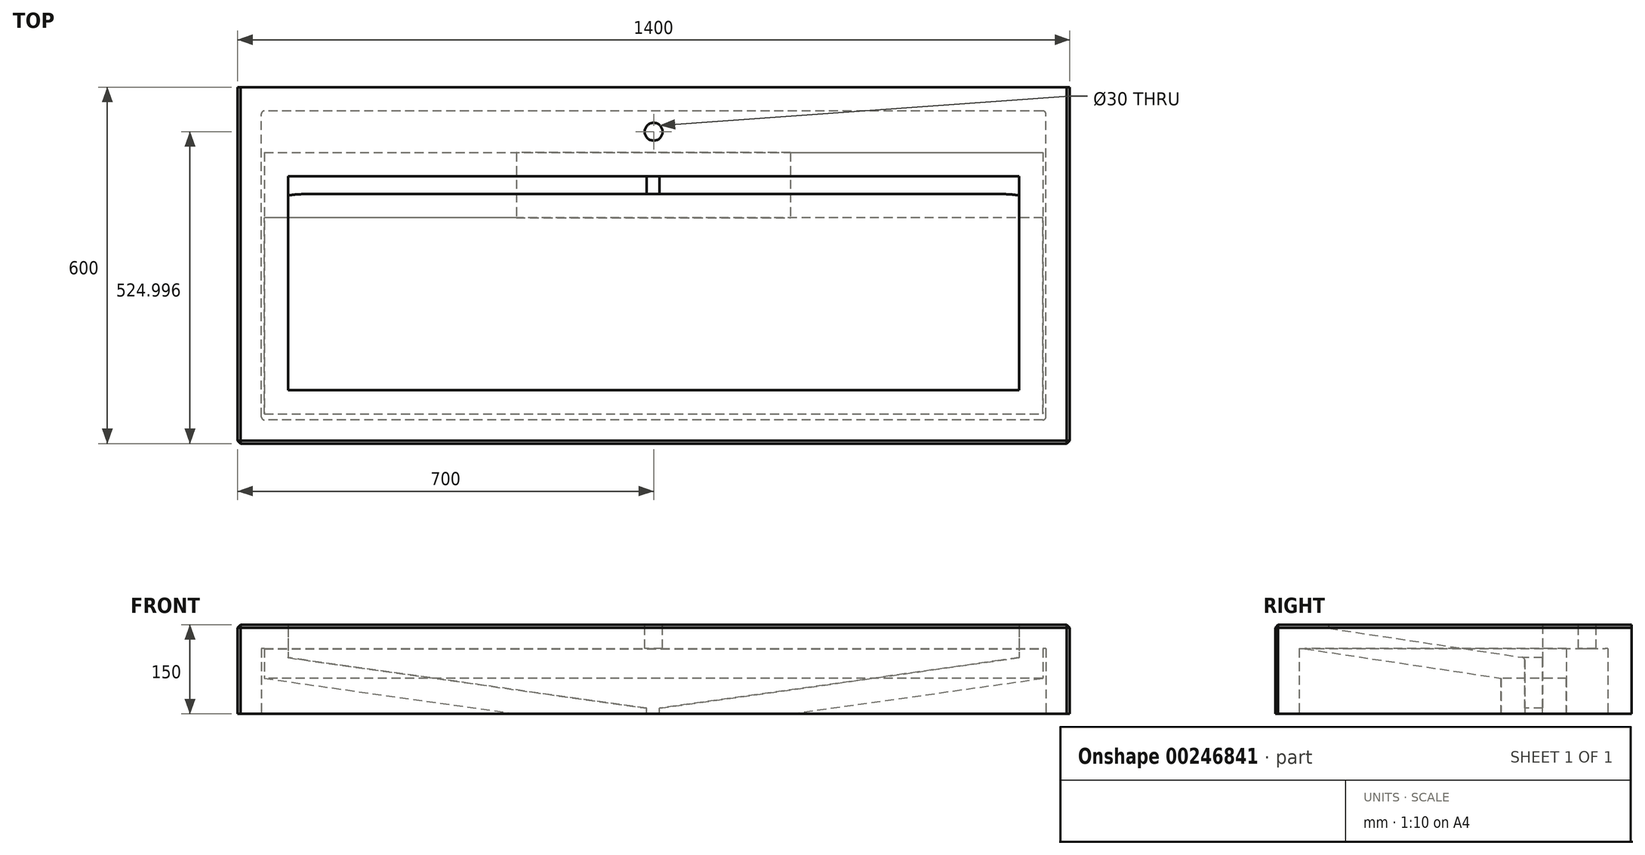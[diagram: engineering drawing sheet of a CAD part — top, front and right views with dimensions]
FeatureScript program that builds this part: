
annotation { "Feature Type Name" : "Feature", "Feature Type Description" : "" }
export const myFeature = defineFeature(function(context is Context, id is Id, definition is map)
    precondition{}
    {
        {
            var Q0;
            Q0=qCreatedBy(makeId("Top.planeOp"),FACE);
            var sketch = newSketch(context, id + "F0", { "sketchPlane" : qUnion([Q0])});
            skLineSegment(sketch, "E0.bottom", {"start": v(700, -284.74) * mm, "end": v(-700, -284.74) * mm});
            skLineSegment(sketch, "E0.top", {"start": v(700, 315.26) * mm, "end": v(-700, 315.26) * mm});
            skLineSegment(sketch, "E0.left", {"start": v(700, -284.74) * mm, "end": v(700, 315.26) * mm});
            skLineSegment(sketch, "E0.right", {"start": v(-700, -284.74) * mm, "end": v(-700, 315.26) * mm});
            skPoint(sketch, "E0.middle", {"position": v(0, 15.26) * mm});
            skSolve(sketch);
        }
        {
            var Q0;
            Q0 = qSketchRegion(id + "F0", true);
            extrude(context, id + "F1", {"entities" : qUnion([Q0]), "depth" : 150 * mm});
        }
        {
            var Q0;
            Q0=makeQuery(id+"F1.opExtrude","CAP_FACE",FACE,{"disambiguationData":[OSD([sQuery(id+"F0.wireOp",EDGE,"E0.bottom"),sQuery(id+"F0.wireOp",EDGE,"E0.top"),sQuery(id+"F0.wireOp",EDGE,"E0.left"),sQuery(id+"F0.wireOp",EDGE,"E0.right")])],"isStart":false});
            var sketch = newSketch(context, id + "F2", { "sketchPlane" : qUnion([Q0])});
            skLineSegment(sketch, "E1.bottom", {"start": v(615, 165.26) * mm, "end": v(-615, 165.26) * mm});
            skLineSegment(sketch, "E1.top", {"start": v(615, -194.74) * mm, "end": v(-615, -194.74) * mm});
            skLineSegment(sketch, "E1.left", {"start": v(615, 165.26) * mm, "end": v(615, -194.74) * mm});
            skLineSegment(sketch, "E1.right", {"start": v(-615, 165.26) * mm, "end": v(-615, -194.74) * mm});
            skLineSegment(sketch, "E2.0", {"start": v(700, 315.26) * mm, "end": v(-700, 315.26) * mm});
            skSolve(sketch);
        }
        {
            var Q0;
            Q0=qCreatedBy(makeId("Right.planeOp"),FACE);
            var Q1;
            Q1=sQuery(id+"F2.wireOp",VERTEX,"E1.bottom.start");
            cPlane(context, id + "F3", {"entities" : qUnion([Q0, Q1]), "cplaneType" : CPlaneType.PLANE_POINT, "offset" : 25 * mm, "width" : 150 * mm, "height" : 150 * mm});
        }
        {
            var Q0;
            Q0=qCreatedBy(id+"F3.planeOp",FACE);
            var sketch = newSketch(context, id + "F4", { "sketchPlane" : qUnion([Q0])});
            skLineSegment(sketch, "E3.0", {"start": v(165.26, 150) * mm, "end": v(-194.74, 150) * mm});
            skLineSegment(sketch, "E4", {"start": v(-194.74, 150) * mm, "end": v(-194.74, 144) * mm});
            skLineSegment(sketch, "E5", {"start": v(165.26, 150) * mm, "end": v(165.26, 90) * mm});
            skLineSegment(sketch, "E6", {"start": v(-194.74, 144) * mm, "end": v(165.26, 90) * mm});
            skSolve(sketch);
        }
        {
            var Q0;
            Q0 = qSketchRegion(id + "F4", true);
            extrude(context, id + "F5", {"entities" : qUnion([Q0]), "operationType" : NewBodyOperationType.REMOVE, "oppositeDirection" : true, "depth" : 1230 * mm});
        }
        {
            var Q0;
            Q0=makeQuery(id+"F2.imprint","IMPRINT",FACE,{"disambiguationData":[TD([[makeQuery(id+"F2.imprint","IMPRINT",EDGE,{"derivedFrom":sQuery(id+"F2.wireOp",EDGE,"E1.bottom")}),1.0]])]});
            var sketch = newSketch(context, id + "F6", { "sketchPlane" : qUnion([Q0])});
            skLineSegment(sketch, "E7.bottom", {"start": v(-615, 165.26) * mm, "end": v(615, 165.26) * mm});
            skLineSegment(sketch, "E7.top", {"start": v(-615, 135.26) * mm, "end": v(615, 135.26) * mm});
            skLineSegment(sketch, "E7.left", {"start": v(-615, 165.26) * mm, "end": v(-615, 135.26) * mm});
            skLineSegment(sketch, "E7.right", {"start": v(615, 165.26) * mm, "end": v(615, 135.26) * mm});
            skSolve(sketch);
        }
        {
            var Q0;
            Q0 = qSketchRegion(id + "F6", true);
            extrude(context, id + "F7", {"entities" : qUnion([Q0]), "operationType" : NewBodyOperationType.REMOVE, "endBound" : BoundingType.THROUGH_ALL, "oppositeDirection" : true, "depth" : 25 * mm});
        }
        {
            var Q0;
            Q0=makeQuery(id+"F7.boolean.opBoolean","COPY",FACE,{"derivedFrom":makeQuery(id+"F7.opExtrude","SWEPT_FACE",FACE,{"disambiguationData":[OSD([sQuery(id+"F6.wireOp",EDGE,"E7.top")])]})});
            var sketch = newSketch(context, id + "F8", { "sketchPlane" : qUnion([Q0])});
            skLineSegment(sketch, "E8", {"start": v(615, 0) * mm, "end": v(12, 0) * mm});
            skLineSegment(sketch, "E9", {"start": v(0, 94.5) * mm, "end": v(0, 9.5) * mm, "construction": true});
            skPoint(sketch, "E9.endSnap0", {"position": v(0, 94.5) * mm});
            skLineSegment(sketch, "E10", {"start": v(-615, 94.5) * mm, "end": v(-10, 9.48) * mm});
            skLineSegment(sketch, "E11", {"start": v(12, 9.5) * mm, "end": v(615, 94.5) * mm});
            skLineSegment(sketch, "E12", {"start": v(12, 9.5) * mm, "end": v(12, 0) * mm});
            skLineSegment(sketch, "E13", {"start": v(-10, 9.48) * mm, "end": v(-10, 0) * mm});
            skLineSegment(sketch, "E14", {"start": v(-615, 0) * mm, "end": v(-10, 0) * mm});
            skLineSegment(sketch, "E15", {"start": v(12, 0) * mm, "end": v(12, 0) * mm});
            skLineSegment(sketch, "E16.0", {"start": v(-615, 94.5) * mm, "end": v(615, 94.5) * mm});
            skLineSegment(sketch, "E17", {"start": v(615, 94.5) * mm, "end": v(615, 0) * mm});
            skLineSegment(sketch, "E18", {"start": v(-615, 94.5) * mm, "end": v(-615, 0) * mm});
            skSolve(sketch);
        }
        {
            var Q0;
            Q0 = qSketchRegion(id + "F8", true);
            var Q1;
            Q1=makeQuery(id+"F7.boolean.opBoolean","MERGE",FACE,{"derivedFrom":[makeQuery(id+"F5.boolean.opBoolean","COPY",FACE,{"derivedFrom":makeQuery(id+"F5.opExtrude","SWEPT_FACE",FACE,{"disambiguationData":[OSD([sQuery(id+"F4.wireOp",EDGE,"E5")])]})}),makeQuery(id+"F7.opExtrude","SWEPT_FACE",FACE,{"disambiguationData":[OSD([sQuery(id+"F6.wireOp",EDGE,"E7.bottom")])]})]});
            extrude(context, id + "F9", {"entities" : qUnion([Q0]), "operationType" : NewBodyOperationType.ADD, "endBound" : BoundingType.UP_TO_SURFACE, "endBoundEntityFace" : qUnion([Q1]), "depth" : 25 * mm});
        }
        {
            var Q0;
            Q0=makeQuery(id+"F9.boolean.opBoolean","MERGE",FACE,{"derivedFrom":[makeQuery(id+"F1.opExtrude","CAP_FACE",FACE,{"disambiguationData":[OSD([sQuery(id+"F0.wireOp",EDGE,"E0.bottom"),sQuery(id+"F0.wireOp",EDGE,"E0.top"),sQuery(id+"F0.wireOp",EDGE,"E0.left"),sQuery(id+"F0.wireOp",EDGE,"E0.right")])],"isStart":true}),makeQuery(id+"F9.opExtrude","SWEPT_FACE",FACE,{"disambiguationData":[OSD([sQuery(id+"F8.wireOp",EDGE,"E8")])]}),makeQuery(id+"F9.opExtrude","SWEPT_FACE",FACE,{"disambiguationData":[OSD([sQuery(id+"F8.wireOp",EDGE,"8b5d63fa-cefd-45bc-85ec-d0f00854f27f.trimOffspring")])]})]});
            shell(context, id + "F10", {"entities" : qUnion([Q0]), "thickness" : 40 * mm});
        }
        {
            var Q0;
            Q0=makeQuery(id+"F5.boolean.opBoolean","COPY",EDGE,{"derivedFrom":makeQuery(id+"F5.opExtrude","CAP_EDGE",EDGE,{"disambiguationData":[OSD([sQuery(id+"F4.wireOp",EDGE,"E3.0")])],"isStart":true})});
            var Q1;
            Q1=makeQuery(id+"F5.boolean.opBoolean","COPY",EDGE,{"derivedFrom":makeQuery(id+"F5.opExtrude","SWEPT_EDGE",EDGE,{"disambiguationData":[OSD([sQuery(id+"F4.wireOp",EDGE,"E3.0"),sQuery(id+"F4.wireOp",EDGE,"E5")])]})});
            var Q2;
            Q2=makeQuery(id+"F5.boolean.opBoolean","COPY",EDGE,{"derivedFrom":makeQuery(id+"F5.opExtrude","SWEPT_EDGE",EDGE,{"disambiguationData":[OSD([sQuery(id+"F4.wireOp",EDGE,"E3.0"),sQuery(id+"F4.wireOp",EDGE,"E4")])]})});
            var Q3;
            Q3=makeQuery(id+"F5.boolean.opBoolean","COPY",EDGE,{"derivedFrom":makeQuery(id+"F5.opExtrude","CAP_EDGE",EDGE,{"disambiguationData":[OSD([sQuery(id+"F4.wireOp",EDGE,"E3.0")])],"isStart":false})});
            var Q4;
            Q4=makeQuery(id+"F1.opExtrude","CAP_EDGE",EDGE,{"disambiguationData":[OSD([sQuery(id+"F0.wireOp",EDGE,"E0.right")])],"isStart":false});
            var Q5;
            Q5=makeQuery(id+"F1.opExtrude","CAP_EDGE",EDGE,{"disambiguationData":[OSD([sQuery(id+"F0.wireOp",EDGE,"E0.bottom")])],"isStart":false});
            var Q6;
            Q6=makeQuery(id+"F1.opExtrude","CAP_EDGE",EDGE,{"disambiguationData":[OSD([sQuery(id+"F0.wireOp",EDGE,"E0.left")])],"isStart":false});
            var Q7;
            Q7=makeQuery(id+"F1.opExtrude","SWEPT_EDGE",EDGE,{"disambiguationData":[OSD([sQuery(id+"F0.wireOp",EDGE,"E0.bottom"),sQuery(id+"F0.wireOp",EDGE,"E0.left")])]});
            var Q8;
            Q8=makeQuery(id+"F1.opExtrude","SWEPT_EDGE",EDGE,{"disambiguationData":[OSD([sQuery(id+"F0.wireOp",EDGE,"E0.bottom"),sQuery(id+"F0.wireOp",EDGE,"E0.right")])]});
            chamfer(context, id + "F11", {"entities" : qUnion([Q0, Q1, Q2, Q3, Q4, Q5, Q6, Q7, Q8]), "width" : 5 * mm, "tangentPropagation" : true});
        }
        {
            var Q0;
            Q0=makeQuery(id+"F2.imprint","IMPRINT",FACE,{"disambiguationData":[TD([[makeQuery(id+"F2.imprint","IMPRINT",EDGE,{"derivedFrom":sQuery(id+"F2.wireOp",EDGE,"E1.bottom")}),-1.0]])]});
            var sketch = newSketch(context, id + "F12", { "sketchPlane" : qUnion([Q0])});
            skLineSegment(sketch, "E19", {"start": v(0, 315.26) * mm, "end": v(0, 240.26) * mm, "construction": true});
            skCircle(sketch, "E20", {"center": v(0, 240.26) * mm, "radius": 15 * mm});
            skSolve(sketch);
        }
        {
            var Q0;
            Q0 = qSketchRegion(id + "F12", true);
            extrude(context, id + "F13", {"entities" : qUnion([Q0]), "operationType" : NewBodyOperationType.REMOVE, "endBound" : BoundingType.THROUGH_ALL, "oppositeDirection" : true, "depth" : 25 * mm});
        }
        {
            var Q0;
            Q0=makeQuery(id+"F10.opShell","OFFSET_EDGE",EDGE,{"disambiguationData":[OSD([sQuery(id+"F0.wireOp",EDGE,"E0.bottom"),sQuery(id+"F0.wireOp",EDGE,"E0.left")])]});
            var Q1;
            Q1=makeQuery(id+"F10.opShell","OFFSET_EDGE",EDGE,{"disambiguationData":[OSD([sQuery(id+"F0.wireOp",EDGE,"E0.top"),sQuery(id+"F0.wireOp",EDGE,"E0.left")])]});
            var Q2;
            Q2=makeQuery(id+"F10.opShell","OFFSET_EDGE",EDGE,{"disambiguationData":[OSD([sQuery(id+"F0.wireOp",EDGE,"E0.bottom"),sQuery(id+"F0.wireOp",EDGE,"E0.right")])]});
            var Q3;
            Q3=makeQuery(id+"F10.opShell","OFFSET_EDGE",EDGE,{"disambiguationData":[OSD([sQuery(id+"F0.wireOp",EDGE,"E0.top"),sQuery(id+"F0.wireOp",EDGE,"E0.right")])]});
            fillet(context, id + "F14", {"entities" : qUnion([Q0, Q1, Q2, Q3]), "radius" : 5 * mm, "tangentPropagation" : true, "allowEdgeOverflow" : false});
        }
        {
            var Q0;
            Q0=makeQuery(id+"F7.boolean.opBoolean","INTERSECT",EDGE,{"derivedFrom":[makeQuery(id+"F5.boolean.opBoolean","COPY",FACE,{"derivedFrom":makeQuery(id+"F5.opExtrude","SWEPT_FACE",FACE,{"disambiguationData":[OSD([sQuery(id+"F4.wireOp",EDGE,"E6")])]})}),makeQuery(id+"F7.opExtrude","SWEPT_FACE",FACE,{"disambiguationData":[OSD([sQuery(id+"F6.wireOp",EDGE,"E7.top")])]})]});
            fillet(context, id + "F15", {"entities" : qUnion([Q0]), "radius" : 5 * mm, "tangentPropagation" : true, "allowEdgeOverflow" : false});
        }
    });
